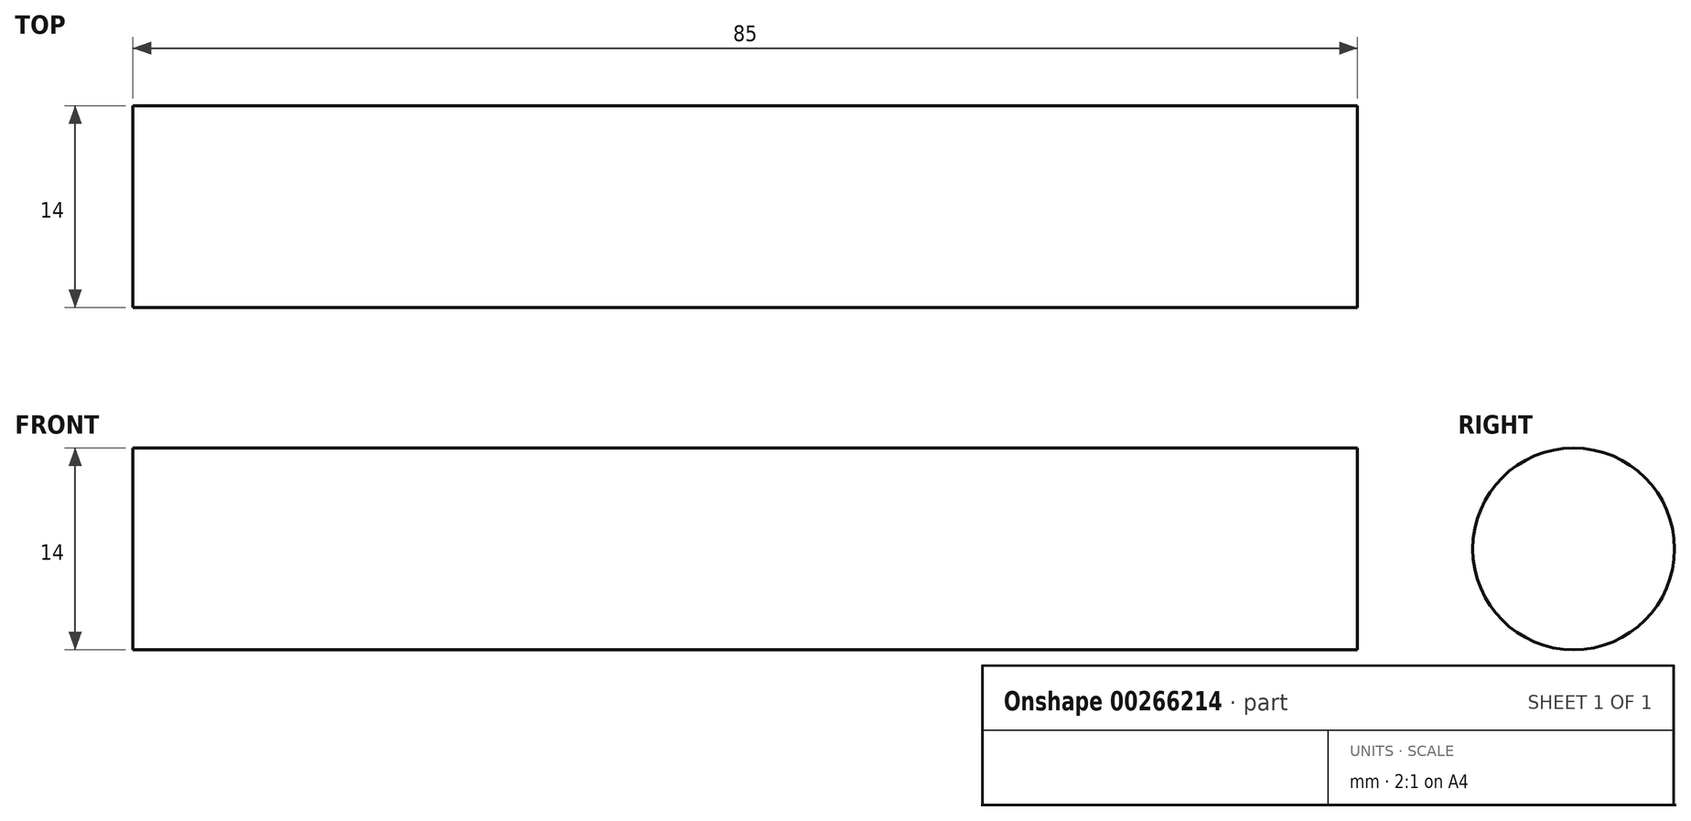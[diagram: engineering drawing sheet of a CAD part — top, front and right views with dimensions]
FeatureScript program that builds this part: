
annotation { "Feature Type Name" : "Feature", "Feature Type Description" : "" }
export const myFeature = defineFeature(function(context is Context, id is Id, definition is map)
    precondition{}
    {
        {
            var Q0;
            Q0=qCreatedBy(makeId("Right.planeOp"),FACE);
            var sketch = newSketch(context, id + "F0", { "sketchPlane" : qUnion([Q0])});
            skCircle(sketch, "E0", {"center": v(0, 0) * mm, "radius": 7 * mm});
            skSolve(sketch);
        }
        {
            var Q0;
            Q0 = qSketchRegion(id + "F0", true);
            extrude(context, id + "F1", {"entities" : qUnion([Q0]), "depth" : 85 * mm});
        }
    });
